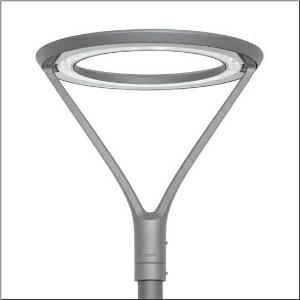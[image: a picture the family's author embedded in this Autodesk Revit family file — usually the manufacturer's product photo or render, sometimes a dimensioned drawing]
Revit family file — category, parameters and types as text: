
# Revit family: dl_r__20_led___p1_0a_5xa512832r008_ef2b
name_source: partatom
category: Lighting Fixtures
units: mm (PartAtom-declared; Revit-internal decimal feet)

## family parameters
Cut with Voids When Loaded = No
Host = Face
Light Source = No
Part Type = Normal
Room Calculation Point = No
Round Connector Dimension = Use Diameter
Shared = No

## types (1)
- --- (1 x LED, 3050 lm, 33.7 W, 2200K)
    Apparent Load = 34 VA
    CIE Flux Codes = 31 71 96 100 100
    Color Rendering = 70
    Color Temperature = 2200K
    Default Elevation = 1800 mm
    Description = DL® 20 LED, mast luminaire, primary light control with cycle path optic, highly specular, primary optical cover: cover, of toughened safety glass of clear glass with excellent transmission level, light distribution: P1.0a, light emission: direct distribution, primary light characteristic: asymmetric, installation type: post-top, LED, High Power LED, rated luminous flux: 3.060lm, luminous efficacy: 86lm/W, light colour: 722, colour temperature: 2200K, control gear: ECG Plus, control: flexible luminous flux parameterisation, time-dependent luminous flux control, constant luminous flux control, digital communication interface, power reduction, overheat protection, electronic power reduction, mains connection: 220..240V, 50/60Hz, connection cable pre-assembled, cable length: 5m, start of lifetime: 36W, end of lifetime: 36W, reduction: 17W, luminaire housing, upper part, of cast aluminium, powder-coated, Siteco® metallic grey (DB 702S), diameter: 690mm, height: 690mm, spigot size: 76mm (post-top), luminaire housing, of cast aluminium, powder-coated, Siteco® metallic grey (DB 702S), protection rating (complete): IP66, insulation class (complete): insulation class II (safety insulation), certification: CE, ENEC, VDE, impact resistance: IK08, permissible operating ambient temperature: -25..+35°C, standard-compliant lighting for roads and squares, packaging unit: 1 piece

Light Distribution: P1.0a
    Height = 690 mm
    Lamp = 1 x LED
    Lamp Light Flux = 3050 lm
    Lamp Power = 33.7 W
    Lamp count = 1
    Length = 690 mm
    Luminous efficacy = 91 lm/W
    Manufacturer = Siteco
    ModVariant = No
    Model = 5XA512832R008
    Number of Poles = 1
    OnlyDefault = Yes
    Power Factor = 1
    Product Name = DL® 20 LED | P1.0a
    Product group = mast luminaire | pylon top
    ProductGroupID = 6100
    Protection Class = Protection class II
    Protection Degree = IP 66
    RLX_Detail_Level = 1
    RlxData = <blob elided: 206913 chars, md5=b58fed72>
    Socket = socket
    Standby Power = 0 W
    System Light Flux = 3050 lm
    System Power = 34 W
    Type Comments = factory setting: luminous flux: 100 % | dim-lin: 254 | 455 mA
    Type Image = l_1006001.jpg
    URL = http://relux.com
    VarID = @adj_118273
    Voltage = 0 V
    Weight = 0.00 kg
    Width = 0 mm  [stored 0 ft]

note: [stored X ft] marks values corroborated as IEEE doubles in the binary element streams (Revit-internal decimal feet)

## geometry (parser evidence)
native form markers: Blend x4, Sweep x11
no freeform markers — native parametric forms only
